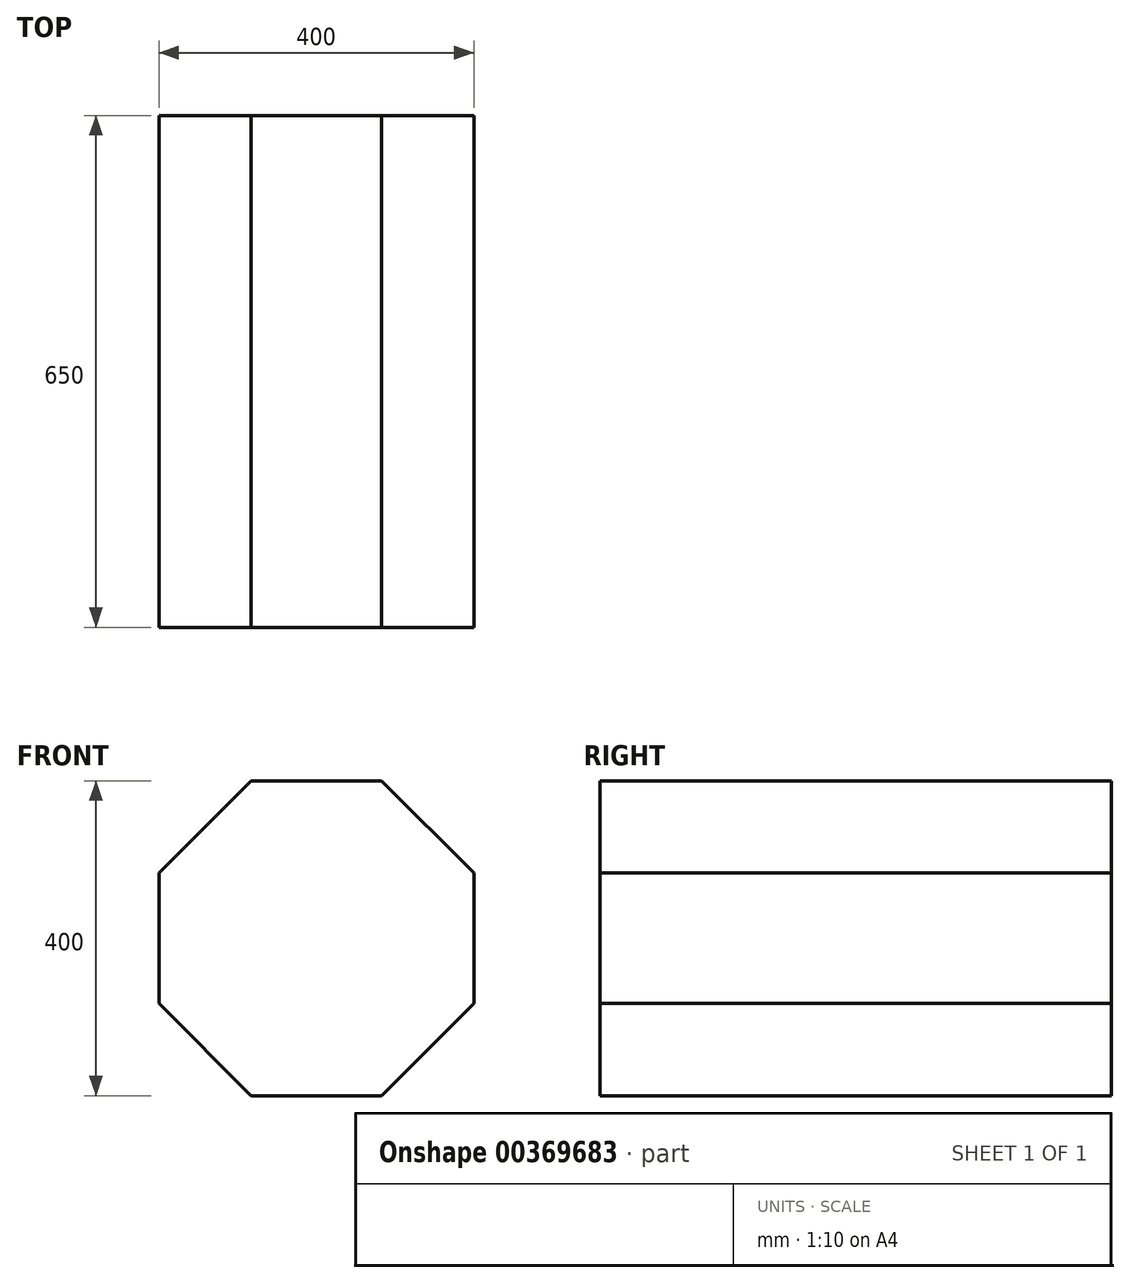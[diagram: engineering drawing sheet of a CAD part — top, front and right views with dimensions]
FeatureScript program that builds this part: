
annotation { "Feature Type Name" : "Feature", "Feature Type Description" : "" }
export const myFeature = defineFeature(function(context is Context, id is Id, definition is map)
    precondition{}
    {
        {
            var Q0;
            Q0=qCreatedBy(makeId("Front.planeOp"),FACE);
            var sketch = newSketch(context, id + "F0", { "sketchPlane" : qUnion([Q0])});
            skLineSegment(sketch, "E0.bottom", {"start": v(0, 0) * mm, "end": v(215.9, 0) * mm});
            skLineSegment(sketch, "E0.top", {"start": v(0, 279.4) * mm, "end": v(215.9, 279.4) * mm});
            skLineSegment(sketch, "E0.left", {"start": v(0, 0) * mm, "end": v(0, 279.4) * mm});
            skLineSegment(sketch, "E0.right", {"start": v(215.9, 0) * mm, "end": v(215.9, 279.4) * mm});
            skArc(sketch, "E1", {"start": v(154.56, 207.7) * mm, "mid": v(108.02, 216.08) * mm, "end": v(61.48, 207.7) * mm});
            skLineSegment(sketch, "E2", {"start": v(61.48, 207.7) * mm, "end": v(154.56, 207.7) * mm, "construction": true});
            skLineSegment(sketch, "E3", {"start": v(108.02, 207.7) * mm, "end": v(108.02, 216.08) * mm, "construction": true});
            skLineSegment(sketch, "E4", {"start": v(108.02, 82.73) * mm, "end": v(61.48, 207.7) * mm});
            skLineSegment(sketch, "E5", {"start": v(108.02, 207.7) * mm, "end": v(108.02, 82.73) * mm});
            skCircle(sketch, "E6.cCircle", {"center": v(572.14, 103.67) * mm, "radius": 200 * mm, "construction": true});
            skLineSegment(sketch, "E6.0", {"start": v(489.3, 303.67) * mm, "end": v(654.98, 303.67) * mm});
            skLineSegment(sketch, "E6.1", {"start": v(654.98, 303.67) * mm, "end": v(772.14, 186.52) * mm});
            skLineSegment(sketch, "E6.2", {"start": v(772.14, 186.52) * mm, "end": v(772.14, 20.83) * mm});
            skLineSegment(sketch, "E6.3", {"start": v(772.14, 20.83) * mm, "end": v(654.98, -96.33) * mm});
            skLineSegment(sketch, "E6.4", {"start": v(654.98, -96.33) * mm, "end": v(489.3, -96.33) * mm});
            skLineSegment(sketch, "E6.5", {"start": v(489.3, -96.33) * mm, "end": v(372.14, 20.83) * mm});
            skLineSegment(sketch, "E6.6", {"start": v(372.14, 20.83) * mm, "end": v(372.14, 186.52) * mm});
            skLineSegment(sketch, "E6.7", {"start": v(372.14, 186.52) * mm, "end": v(489.3, 303.67) * mm});
            skPoint(sketch, "E6.0.midPoint", {"position": v(572.14, 303.67) * mm});
            skSolve(sketch);
        }
        {
            var Q0;
            Q0=makeQuery(id+"F0.imprint","IMPRINT",FACE,{"disambiguationData":[TD([[makeQuery(id+"F0.imprint","IMPRINT",EDGE,{"derivedFrom":sQuery(id+"F0.wireOp",EDGE,"E6.0")}),-1.0]])]});
            extrude(context, id + "F1", {"entities" : qUnion([Q0]), "depth" : 650 * mm});
        }
    });
